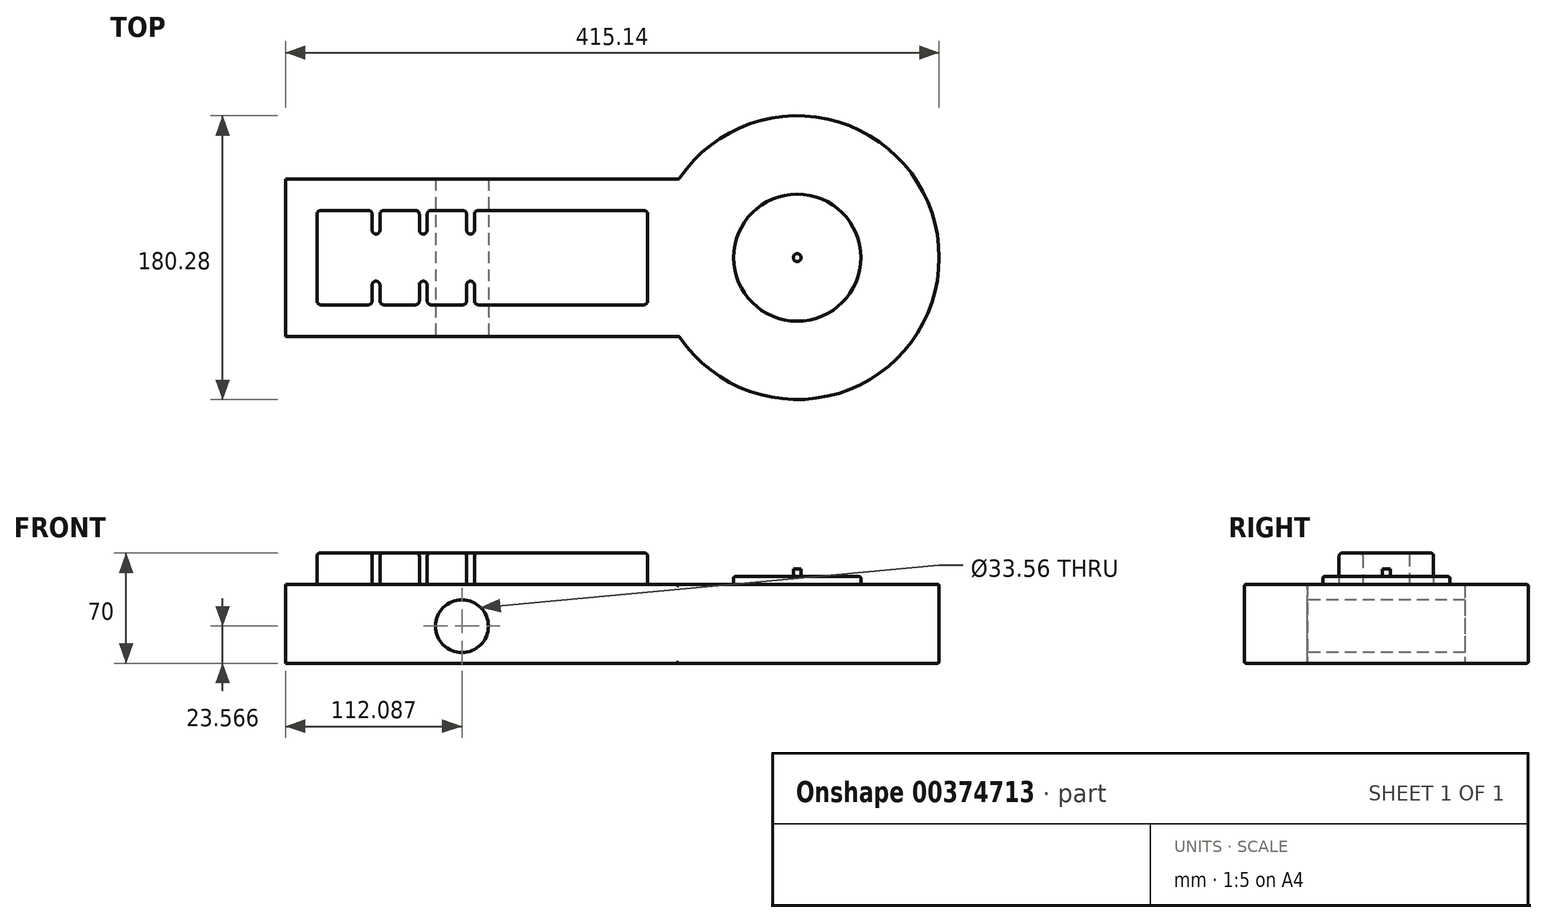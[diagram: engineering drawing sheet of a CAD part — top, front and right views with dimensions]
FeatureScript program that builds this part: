
annotation { "Feature Type Name" : "Feature", "Feature Type Description" : "" }
export const myFeature = defineFeature(function(context is Context, id is Id, definition is map)
    precondition{}
    {
        {
            var Q0;
            Q0=qCreatedBy(makeId("Top.planeOp"),FACE);
            var sketch = newSketch(context, id + "F0", { "sketchPlane" : qUnion([Q0])});
            skLineSegment(sketch, "E0.bottom", {"start": v(0, 0) * mm, "end": v(250, 0) * mm});
            skLineSegment(sketch, "E0.top", {"start": v(0, 100) * mm, "end": v(250, 100) * mm});
            skLineSegment(sketch, "E0.left", {"start": v(0, 0) * mm, "end": v(0, 100) * mm});
            skLineSegment(sketch, "E0.right", {"start": v(250, 0) * mm, "end": v(250, 100) * mm});
            skArc(sketch, "E1", {"start": v(250, 0) * mm, "mid": v(415.14, 50) * mm, "end": v(250, 100) * mm});
            skSolve(sketch);
        }
        {
            var Q0;
            Q0=makeQuery(id+"F0.imprint","IMPRINT",FACE,{"disambiguationData":[TD([[makeQuery(id+"F0.imprint","IMPRINT",EDGE,{"derivedFrom":sQuery(id+"F0.wireOp",EDGE,"E0.bottom")}),1.0]])]});
            var Q1;
            Q1=makeQuery(id+"F0.imprint","IMPRINT",FACE,{"disambiguationData":[TD([[makeQuery(id+"F0.imprint","IMPRINT",EDGE,{"derivedFrom":sQuery(id+"F0.wireOp",EDGE,"E0.right")}),-1.0]])]});
            extrude(context, id + "F1", {"entities" : qUnion([Q0, Q1]), "depth" : 50 * mm});
        }
        {
            var Q0;
            Q0=makeQuery(id+"F1.opExtrude","CAP_FACE",FACE,{"disambiguationData":[OSD([sQuery(id+"F0.wireOp",EDGE,"E0.bottom"),sQuery(id+"F0.wireOp",EDGE,"E0.top"),sQuery(id+"F0.wireOp",EDGE,"E0.left"),sQuery(id+"F0.wireOp",EDGE,"E1")])],"isStart":false});
            var sketch = newSketch(context, id + "F2", { "sketchPlane" : qUnion([Q0])});
            skLineSegment(sketch, "E2.bottom", {"start": v(20, 80) * mm, "end": v(230, 80) * mm});
            skLineSegment(sketch, "E2.top", {"start": v(20, 20) * mm, "end": v(230, 20) * mm});
            skLineSegment(sketch, "E2.left", {"start": v(20, 80) * mm, "end": v(20, 20) * mm});
            skLineSegment(sketch, "E2.right", {"start": v(230, 80) * mm, "end": v(230, 20) * mm});
            skLineSegment(sketch, "E3.bottom", {"start": v(55, 80) * mm, "end": v(60, 80) * mm});
            skLineSegment(sketch, "E3.top", {"start": v(55, 65) * mm, "end": v(60, 65) * mm});
            skLineSegment(sketch, "E3.left", {"start": v(55, 80) * mm, "end": v(55, 65) * mm});
            skLineSegment(sketch, "E3.right", {"start": v(60, 80) * mm, "end": v(60, 65) * mm});
            skLineSegment(sketch, "E4.bottom", {"start": v(85, 80) * mm, "end": v(90, 80) * mm});
            skLineSegment(sketch, "E4.top", {"start": v(85, 65) * mm, "end": v(90, 65) * mm});
            skLineSegment(sketch, "E4.left", {"start": v(85, 80) * mm, "end": v(85, 65) * mm});
            skLineSegment(sketch, "E4.right", {"start": v(90, 80) * mm, "end": v(90, 65) * mm});
            skLineSegment(sketch, "E5.bottom", {"start": v(115, 80) * mm, "end": v(120, 80) * mm});
            skLineSegment(sketch, "E5.top", {"start": v(115, 65) * mm, "end": v(120, 65) * mm});
            skLineSegment(sketch, "E5.left", {"start": v(115, 80) * mm, "end": v(115, 65) * mm});
            skLineSegment(sketch, "E5.right", {"start": v(120, 80) * mm, "end": v(120, 65) * mm});
            skLineSegment(sketch, "E6.bottom", {"start": v(55, 20) * mm, "end": v(60, 20) * mm});
            skLineSegment(sketch, "E6.top", {"start": v(55, 35) * mm, "end": v(60, 35) * mm});
            skLineSegment(sketch, "E6.left", {"start": v(55, 20) * mm, "end": v(55, 35) * mm});
            skLineSegment(sketch, "E6.right", {"start": v(60, 20) * mm, "end": v(60, 35) * mm});
            skLineSegment(sketch, "E7.bottom", {"start": v(85, 20) * mm, "end": v(90, 20) * mm});
            skLineSegment(sketch, "E7.top", {"start": v(85, 35) * mm, "end": v(90, 35) * mm});
            skLineSegment(sketch, "E7.left", {"start": v(85, 20) * mm, "end": v(85, 35) * mm});
            skLineSegment(sketch, "E7.right", {"start": v(90, 20) * mm, "end": v(90, 35) * mm});
            skLineSegment(sketch, "E8.bottom", {"start": v(115, 20) * mm, "end": v(120, 20) * mm});
            skLineSegment(sketch, "E8.top", {"start": v(115, 35) * mm, "end": v(120, 35) * mm});
            skLineSegment(sketch, "E8.left", {"start": v(115, 20) * mm, "end": v(115, 35) * mm});
            skLineSegment(sketch, "E8.right", {"start": v(120, 20) * mm, "end": v(120, 35) * mm});
            skSolve(sketch);
        }
        {
            var Q0;
            {var subQ20=sQuery(id+"F2.wireOp",EDGE,"E2.left");Q0=makeQuery(id+"F2.imprint","IMPRINT",FACE,{"disambiguationData":[TD([[makeQuery(id+"F2.imprint","IMPRINT",EDGE,{"derivedFrom":subQ20}),1.0]])]});}
            extrude(context, id + "F3", {"entities" : qUnion([Q0]), "operationType" : NewBodyOperationType.ADD, "depth" : 20 * mm});
        }
        {
            var Q0;
            Q0=makeQuery(id+"F1.opExtrude","CAP_FACE",FACE,{"disambiguationData":[OSD([sQuery(id+"F0.wireOp",EDGE,"E0.bottom"),sQuery(id+"F0.wireOp",EDGE,"E0.top"),sQuery(id+"F0.wireOp",EDGE,"E0.left"),sQuery(id+"F0.wireOp",EDGE,"E1")])],"isStart":false});
            var sketch = newSketch(context, id + "F4", { "sketchPlane" : qUnion([Q0])});
            skCircle(sketch, "E9", {"center": v(325, 50) * mm, "radius": 40.38 * mm});
            skSolve(sketch);
        }
        {
            var Q0;
            Q0=qSketchRegion(id+"F4",true);
            extrude(context, id + "F5", {"entities" : qUnion([Q0]), "operationType" : NewBodyOperationType.ADD, "depth" : 5 * mm});
        }
        {
            var Q0;
            Q0=makeQuery(id+"F5.opExtrude","CAP_FACE",FACE,{"disambiguationData":[OSD([sQuery(id+"F4.wireOp",EDGE,"E9")])],"isStart":false});
            var sketch = newSketch(context, id + "F6", { "sketchPlane" : qUnion([Q0])});
            skCircle(sketch, "E10", {"center": v(325, 50) * mm, "radius": 2.5 * mm});
            skSolve(sketch);
        }
        {
            var Q0;
            Q0=makeQuery(id+"F6.imprint","IMPRINT",FACE,{"disambiguationData":[TD([[makeQuery(id+"F6.imprint","IMPRINT",EDGE,{"derivedFrom":sQuery(id+"F6.wireOp",EDGE,"E10")}),1.0]])]});
            extrude(context, id + "F7", {"entities" : qUnion([Q0]), "operationType" : NewBodyOperationType.ADD, "depth" : 5 * mm});
        }
        {
            var Q0;
            Q0=makeQuery(id+"F1.opExtrude","SWEPT_FACE",FACE,{"disambiguationData":[OSD([sQuery(id+"F0.wireOp",EDGE,"E1")])]});
            var Q1;
            Q1=makeQuery(id+"F5.opExtrude","CAP_EDGE",EDGE,{"disambiguationData":[OSD([sQuery(id+"F4.wireOp",EDGE,"E9")])],"isStart":false});
            var Q2;
            Q2=makeQuery(id+"F5.opExtrude","CAP_EDGE",EDGE,{"disambiguationData":[OSD([sQuery(id+"F4.wireOp",EDGE,"E9")])],"isStart":true});
            fillet(context, id + "F8", {"entities" : qUnion([Q0, Q1, Q2]), "radius" : 1 * mm, "tangentPropagation" : true, "allowEdgeOverflow" : false});
        }
        {
            var Q0;
            Q0=makeQuery(id+"F3.opExtrude","SWEPT_EDGE",EDGE,{"disambiguationData":[OSD([sQuery(id+"F2.wireOp",EDGE,"E6.top"),sQuery(id+"F2.wireOp",EDGE,"E6.left")])]});
            var Q1;
            Q1=makeQuery(id+"F3.opExtrude","SWEPT_EDGE",EDGE,{"disambiguationData":[OSD([sQuery(id+"F2.wireOp",EDGE,"E2.top"),sQuery(id+"F2.wireOp",EDGE,"E6.bottom"),sQuery(id+"F2.wireOp",EDGE,"E6.left")])]});
            var Q2;
            Q2=makeQuery(id+"F3.opExtrude","SWEPT_EDGE",EDGE,{"disambiguationData":[OSD([sQuery(id+"F2.wireOp",EDGE,"E6.top"),sQuery(id+"F2.wireOp",EDGE,"E6.right")])]});
            var Q3;
            Q3=makeQuery(id+"F3.opExtrude","SWEPT_EDGE",EDGE,{"disambiguationData":[OSD([sQuery(id+"F2.wireOp",EDGE,"E2.top"),sQuery(id+"F2.wireOp",EDGE,"E6.bottom"),sQuery(id+"F2.wireOp",EDGE,"E6.right")])]});
            var Q4;
            Q4=makeQuery(id+"F3.opExtrude","SWEPT_EDGE",EDGE,{"disambiguationData":[OSD([sQuery(id+"F2.wireOp",EDGE,"E2.top"),sQuery(id+"F2.wireOp",EDGE,"E7.bottom"),sQuery(id+"F2.wireOp",EDGE,"E7.left")])]});
            var Q5;
            Q5=makeQuery(id+"F3.opExtrude","SWEPT_EDGE",EDGE,{"disambiguationData":[OSD([sQuery(id+"F2.wireOp",EDGE,"E7.top"),sQuery(id+"F2.wireOp",EDGE,"E7.right")])]});
            var Q6;
            Q6=makeQuery(id+"F3.opExtrude","SWEPT_EDGE",EDGE,{"disambiguationData":[OSD([sQuery(id+"F2.wireOp",EDGE,"E2.top"),sQuery(id+"F2.wireOp",EDGE,"E7.bottom"),sQuery(id+"F2.wireOp",EDGE,"E7.right")])]});
            var Q7;
            Q7=makeQuery(id+"F3.opExtrude","SWEPT_EDGE",EDGE,{"disambiguationData":[OSD([sQuery(id+"F2.wireOp",EDGE,"E2.top"),sQuery(id+"F2.wireOp",EDGE,"E8.bottom"),sQuery(id+"F2.wireOp",EDGE,"E8.left")])]});
            var Q8;
            Q8=makeQuery(id+"F3.opExtrude","SWEPT_EDGE",EDGE,{"disambiguationData":[OSD([sQuery(id+"F2.wireOp",EDGE,"E8.top"),sQuery(id+"F2.wireOp",EDGE,"E8.right")])]});
            var Q9;
            Q9=makeQuery(id+"F3.opExtrude","SWEPT_EDGE",EDGE,{"disambiguationData":[OSD([sQuery(id+"F2.wireOp",EDGE,"E2.top"),sQuery(id+"F2.wireOp",EDGE,"E8.bottom"),sQuery(id+"F2.wireOp",EDGE,"E8.right")])]});
            var Q10;
            Q10=makeQuery(id+"F3.opExtrude","SWEPT_EDGE",EDGE,{"disambiguationData":[OSD([sQuery(id+"F2.wireOp",EDGE,"E7.top"),sQuery(id+"F2.wireOp",EDGE,"E7.left")])]});
            var Q11;
            Q11=makeQuery(id+"F3.opExtrude","SWEPT_EDGE",EDGE,{"disambiguationData":[OSD([sQuery(id+"F2.wireOp",EDGE,"E8.top"),sQuery(id+"F2.wireOp",EDGE,"E8.left")])]});
            var Q12;
            Q12=makeQuery(id+"F3.opExtrude","SWEPT_EDGE",EDGE,{"disambiguationData":[OSD([sQuery(id+"F2.wireOp",EDGE,"E3.top"),sQuery(id+"F2.wireOp",EDGE,"E3.left")])]});
            var Q13;
            Q13=makeQuery(id+"F3.opExtrude","SWEPT_EDGE",EDGE,{"disambiguationData":[OSD([sQuery(id+"F2.wireOp",EDGE,"E2.bottom"),sQuery(id+"F2.wireOp",EDGE,"E3.bottom"),sQuery(id+"F2.wireOp",EDGE,"E3.left")])]});
            var Q14;
            Q14=makeQuery(id+"F3.opExtrude","SWEPT_EDGE",EDGE,{"disambiguationData":[OSD([sQuery(id+"F2.wireOp",EDGE,"E4.top"),sQuery(id+"F2.wireOp",EDGE,"E4.left")])]});
            var Q15;
            Q15=makeQuery(id+"F3.opExtrude","SWEPT_EDGE",EDGE,{"disambiguationData":[OSD([sQuery(id+"F2.wireOp",EDGE,"E2.bottom"),sQuery(id+"F2.wireOp",EDGE,"E4.bottom"),sQuery(id+"F2.wireOp",EDGE,"E4.left")])]});
            var Q16;
            Q16=makeQuery(id+"F3.opExtrude","SWEPT_EDGE",EDGE,{"disambiguationData":[OSD([sQuery(id+"F2.wireOp",EDGE,"E5.top"),sQuery(id+"F2.wireOp",EDGE,"E5.left")])]});
            var Q17;
            Q17=makeQuery(id+"F3.opExtrude","SWEPT_EDGE",EDGE,{"disambiguationData":[OSD([sQuery(id+"F2.wireOp",EDGE,"E2.bottom"),sQuery(id+"F2.wireOp",EDGE,"E5.bottom"),sQuery(id+"F2.wireOp",EDGE,"E5.left")])]});
            var Q18;
            Q18=makeQuery(id+"F3.opExtrude","SWEPT_EDGE",EDGE,{"disambiguationData":[OSD([sQuery(id+"F2.wireOp",EDGE,"E3.top"),sQuery(id+"F2.wireOp",EDGE,"E3.right")])]});
            var Q19;
            Q19=makeQuery(id+"F3.opExtrude","SWEPT_EDGE",EDGE,{"disambiguationData":[OSD([sQuery(id+"F2.wireOp",EDGE,"E2.bottom"),sQuery(id+"F2.wireOp",EDGE,"E3.bottom"),sQuery(id+"F2.wireOp",EDGE,"E3.right")])]});
            var Q20;
            Q20=makeQuery(id+"F3.opExtrude","SWEPT_EDGE",EDGE,{"disambiguationData":[OSD([sQuery(id+"F2.wireOp",EDGE,"E4.top"),sQuery(id+"F2.wireOp",EDGE,"E4.right")])]});
            var Q21;
            Q21=makeQuery(id+"F3.opExtrude","SWEPT_EDGE",EDGE,{"disambiguationData":[OSD([sQuery(id+"F2.wireOp",EDGE,"E2.bottom"),sQuery(id+"F2.wireOp",EDGE,"E4.bottom"),sQuery(id+"F2.wireOp",EDGE,"E4.right")])]});
            var Q22;
            Q22=makeQuery(id+"F3.opExtrude","SWEPT_EDGE",EDGE,{"disambiguationData":[OSD([sQuery(id+"F2.wireOp",EDGE,"E5.top"),sQuery(id+"F2.wireOp",EDGE,"E5.right")])]});
            var Q23;
            Q23=makeQuery(id+"F3.opExtrude","SWEPT_EDGE",EDGE,{"disambiguationData":[OSD([sQuery(id+"F2.wireOp",EDGE,"E2.bottom"),sQuery(id+"F2.wireOp",EDGE,"E5.bottom"),sQuery(id+"F2.wireOp",EDGE,"E5.right")])]});
            var Q24;
            Q24=makeQuery(id+"F3.opExtrude","SWEPT_EDGE",EDGE,{"disambiguationData":[OSD([sQuery(id+"F2.wireOp",EDGE,"E2.bottom"),sQuery(id+"F2.wireOp",EDGE,"E2.left")])]});
            var Q25;
            Q25=makeQuery(id+"F3.opExtrude","SWEPT_EDGE",EDGE,{"disambiguationData":[OSD([sQuery(id+"F2.wireOp",EDGE,"E2.top"),sQuery(id+"F2.wireOp",EDGE,"E2.left")])]});
            var Q26;
            Q26=makeQuery(id+"F3.opExtrude","SWEPT_EDGE",EDGE,{"disambiguationData":[OSD([sQuery(id+"F2.wireOp",EDGE,"E2.bottom"),sQuery(id+"F2.wireOp",EDGE,"E2.right")])]});
            var Q27;
            Q27=makeQuery(id+"F3.opExtrude","SWEPT_EDGE",EDGE,{"disambiguationData":[OSD([sQuery(id+"F2.wireOp",EDGE,"E2.top"),sQuery(id+"F2.wireOp",EDGE,"E2.right")])]});
            fillet(context, id + "F9", {"entities" : qUnion([Q0, Q1, Q2, Q3, Q4, Q5, Q6, Q7, Q8, Q9, Q10, Q11, Q12, Q13, Q14, Q15, Q16, Q17, Q18, Q19, Q20, Q21, Q22, Q23, Q24, Q25, Q26, Q27]), "radius" : 2.5 * mm, "tangentPropagation" : true, "allowEdgeOverflow" : false});
        }
        {
            var Q0;
            {var subQ0=sQuery(id+"F2.wireOp",EDGE,"E2.bottom");Q0=makeQuery(id+"F3.opExtrude","CAP_EDGE",EDGE,{"disambiguationData":[OSD([subQ0]),TDD([makeQuery(id+"F2.imprint","IMPRINT",EDGE,{"disambiguationData":[TD([[makeQuery(id+"F2.imprint","INTERSECT",VERTEX,{"derivedFrom":[subQ0,sQuery(id+"F2.wireOp",EDGE,"E2.right")]}),1.0]])],"derivedFrom":subQ0})])],"isStart":false});}
            var Q1;
            Q1=makeQuery(id+"F3.opExtrude","CAP_EDGE",EDGE,{"disambiguationData":[OSD([sQuery(id+"F2.wireOp",EDGE,"E2.right")])],"isStart":false});
            fillet(context, id + "F10", {"entities" : qUnion([Q0, Q1]), "radius" : 2 * mm, "tangentPropagation" : true, "allowEdgeOverflow" : false});
        }
        {
            var Q0;
            Q0=makeQuery(id+"F1.opExtrude","SWEPT_FACE",FACE,{"disambiguationData":[OSD([sQuery(id+"F0.wireOp",EDGE,"E0.bottom")])]});
            var sketch = newSketch(context, id + "F11", { "sketchPlane" : qUnion([Q0])});
            skCircle(sketch, "E11", {"center": v(112.09, 23.57) * mm, "radius": 16.78 * mm});
            skSolve(sketch);
        }
        {
            var Q0;
            Q0 = qSketchRegion(id + "F11", true);
            extrude(context, id + "F12", {"entities" : qUnion([Q0]), "operationType" : NewBodyOperationType.REMOVE, "endBound" : BoundingType.THROUGH_ALL, "oppositeDirection" : true, "depth" : 25 * mm});
        }
    });
